FCSTD DOCUMENT  (FreeCAD 0.21R33771 (Git))
Label: tc2-sim-usb-pi3-boarder
License: All rights reserved
LicenseURL: https://en.wikipedia.org/wiki/All_rights_reserved
objects: Sketcher::SketchObject×1
note: 1 computed .brp shape members not serialized (recipe doc carries the construction recipe); baked Part::Feature solids carry a one-line shape summary decoded from their .brp

FEATURE [Sketcher::SketchObject] Sketch
  FullyConstrained = true
  sketch-geometry (11):
    g0: LineSegment StartX=-1.5 StartY=6 StartZ=0 EndX=21 EndY=6 EndZ=0
    g1: LineSegment StartX=21 StartY=6 StartZ=0 EndX=21 EndY=-22 EndZ=0
    g2: LineSegment StartX=21 StartY=-22 StartZ=0 EndX=-1.5 EndY=-22 EndZ=0
    g3: LineSegment StartX=-1.5 StartY=-22 StartZ=0 EndX=-1.5 EndY=6 EndZ=0
    g4: LineSegment StartX=21 StartY=-22 StartZ=0 EndX=21 EndY=-21.0487 EndZ=0
    g5: LineSegment StartX=20.145 StartY=-18.9513 StartZ=0 EndX=20.145 EndY=-12.0487 EndZ=0
    g6: LineSegment StartX=21 StartY=-9.95131 StartZ=0 EndX=21 EndY=6 EndZ=0
    g7: ArcOfCircle CenterX=19.5 CenterY=-9.95131 CenterZ=0 NormalX=0 NormalY=0 NormalZ=1 AngleXU=0 Radius=1.5 StartAngle=5.50901 EndAngle=6.28319
    g8: ArcOfCircle CenterX=21.645 CenterY=-12.0487 CenterZ=0 NormalX=0 NormalY=0 NormalZ=1 AngleXU=0 Radius=1.5 StartAngle=2.36742 EndAngle=3.14159
    g9: ArcOfCircle CenterX=21.645 CenterY=-18.9513 CenterZ=0 NormalX=0 NormalY=0 NormalZ=1 AngleXU=0 Radius=1.5 StartAngle=3.14159 EndAngle=3.91576
    g10: ArcOfCircle CenterX=19.5 CenterY=-21.0487 CenterZ=0 NormalX=0 NormalY=0 NormalZ=1 AngleXU=0 Radius=1.5 StartAngle=1e-15 EndAngle=0.774172
  constraints (30):
    c: Coincident(g0,g1)
    c: Coincident(g1,g2)
    c: Coincident(g2,g3)
    c: Coincident(g3,g0)
    c: Horizontal(g0)
    c: Horizontal(g2)
    c: Vertical(g1)
    c: Vertical(g3)
    c: DistanceX(g0,g-1) = 1.5
    c: DistanceY(g-1,g0) = 6
    c: DistanceX(g-1,g0) = 21
    c: DistanceY(g2,g-1) = 22
    c: Coincident(g2,g4)
    c: Vertical(g5)
    c: Coincident(g6,g0)
    c: Tangent(g6,g7) = -1.5708
    c: Tangent(g5,g8) = 1.5708
    c: Tangent(g5,g9) = 1.5708
    c: Tangent(g4,g10) = -1.5708
    c: Equal(g10,g9)
    c: Equal(g10,g8)
    c: Equal(g10,g7)
    c: Radius(g10) = 1.5
    c: Vertical(g4)
    c: Vertical(g6)
    c: Tangent(g9,g10) = 1.5708
    c: Tangent(g8,g7) = 1.5708
    c: DistanceY(g7,g-1) = 11
    c: DistanceY(g9,g-1) = 20
    c: DistanceX(g-1,g5) = 20.145
